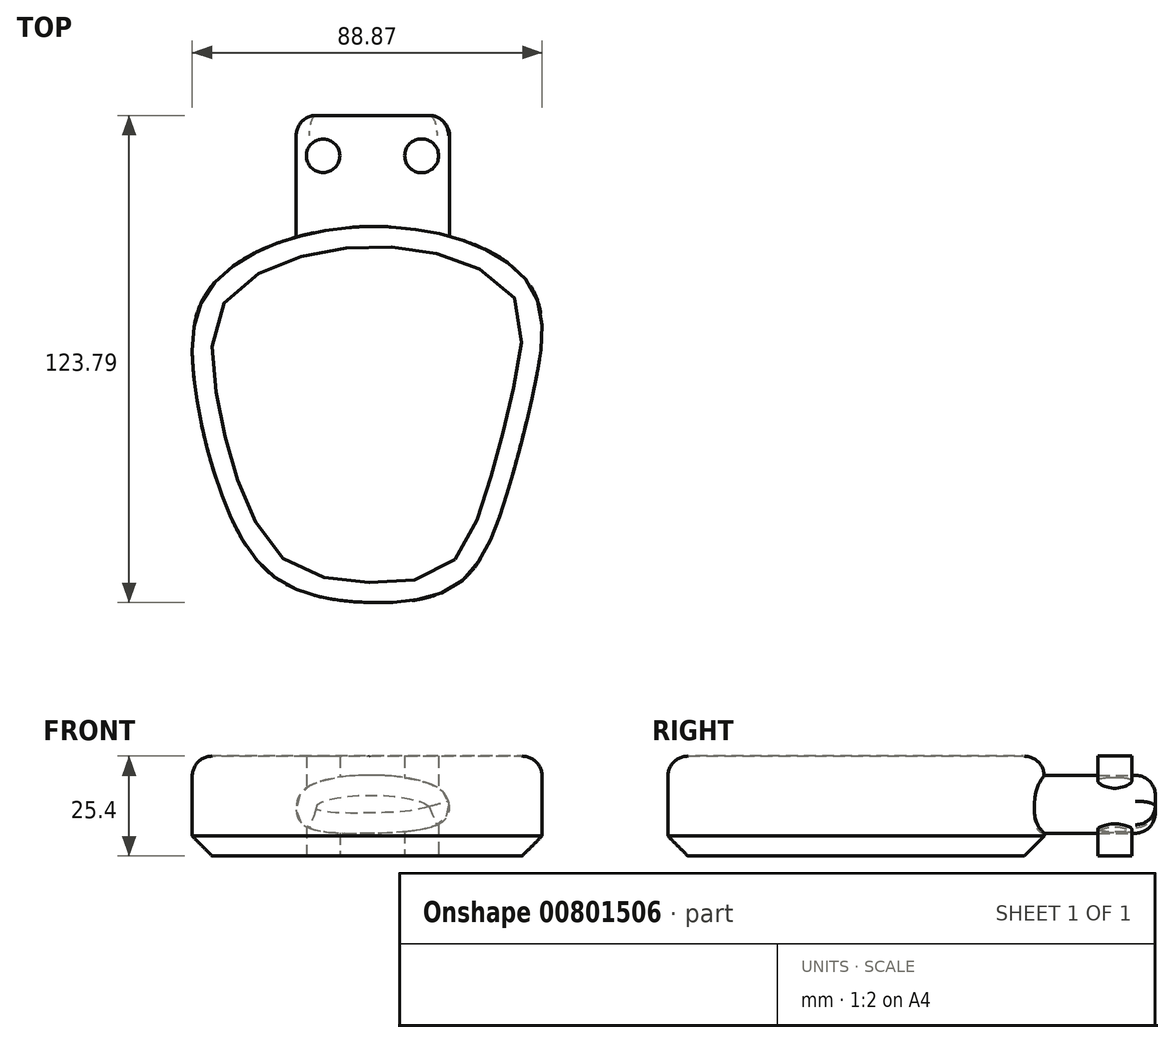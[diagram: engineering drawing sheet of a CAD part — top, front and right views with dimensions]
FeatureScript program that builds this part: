
annotation { "Feature Type Name" : "Feature", "Feature Type Description" : "" }
export const myFeature = defineFeature(function(context is Context, id is Id, definition is map)
    precondition{}
    {
        {
            var Q0;
            Q0=qCreatedBy(makeId("Top.planeOp"),FACE);
            var sketch = newSketch(context, id + "F0", { "sketchPlane" : qUnion([Q0])});
            skFitSpline(sketch, "E0", {"points": [v(0, -55.93) * mm, v(-24.36, -49.12) * mm, v(-38.24, -25.99) * mm, v(-44.22, 0) * mm, v(-40.41, 23.81) * mm, v(0, 39.6) * mm, v(40.69, 25.17) * mm, v(42.32, 0) * mm, v(34.97, -28.71) * mm, v(23.27, -50.75) * mm, v(0, -55.93) * mm]});
            skSolve(sketch);
        }
        {
            var Q0;
            Q0=makeQuery(id+"F0.imprint","IMPRINT",FACE,{"disambiguationData":[TD([[makeQuery(id+"F0.imprint","IMPRINT",EDGE,{"derivedFrom":sQuery(id+"F0.wireOp",EDGE,"E0")}),-1.0]])]});
            extrude(context, id + "F1", {"entities" : qUnion([Q0]), "depth" : 25.4 * mm, "offsetDistance" : 25.4 * mm});
        }
        {
            var Q0;
            Q0=makeQuery(id+"F1.opExtrude","CAP_EDGE",EDGE,{"disambiguationData":[OSD([sQuery(id+"F0.wireOp",EDGE,"E0")])],"isStart":false});
            fillet(context, id + "F2", {"entities" : qUnion([Q0]), "radius" : 5.08 * mm, "tangentPropagation" : true, "allowEdgeOverflow" : false});
        }
        {
            var Q0;
            Q0=makeQuery(id+"F1.opExtrude","CAP_EDGE",EDGE,{"disambiguationData":[OSD([sQuery(id+"F0.wireOp",EDGE,"E0")])],"isStart":true});
            chamfer(context, id + "F3", {"entities" : qUnion([Q0]), "width" : 5.08 * mm, "tangentPropagation" : true});
        }
        {
            var Q0;
            Q0=qCreatedBy(makeId("Front.planeOp"),FACE);
            var sketch = newSketch(context, id + "F4", { "sketchPlane" : qUnion([Q0])});
            skFitSpline(sketch, "E1", {"points": [v(0, 20.55) * mm, v(16.74, 17.83) * mm, v(20.27, 14.02) * mm, v(19.19, 9.12) * mm, v(0, 5.85) * mm, v(-16.74, 8.03) * mm, v(-18.37, 12.65) * mm, v(-15.92, 17.28) * mm, v(0, 20.55) * mm]});
            skSolve(sketch);
        }
        {
            var Q0;
            Q0 = qSketchRegion(id + "F4", true);
            extrude(context, id + "F5", {"entities" : qUnion([Q0]), "operationType" : NewBodyOperationType.ADD, "oppositeDirection" : true, "depth" : 67.82 * mm, "offsetDistance" : 25.4 * mm});
        }
        {
            var Q0;
            Q0=makeQuery(id+"F5.opExtrude","CAP_EDGE",EDGE,{"disambiguationData":[OSD([sQuery(id+"F4.wireOp",EDGE,"E1")])],"isStart":false});
            fillet(context, id + "F6", {"entities" : qUnion([Q0]), "radius" : 5.08 * mm, "tangentPropagation" : true, "allowEdgeOverflow" : false});
        }
        {
            var Q0;
            Q0=qCreatedBy(makeId("Top.planeOp"),FACE);
            var sketch = newSketch(context, id + "F7", { "sketchPlane" : qUnion([Q0])});
            skCircle(sketch, "E2", {"center": v(-11.57, 57.56) * mm, "radius": 4.25 * mm});
            skSolve(sketch);
        }
        {
            var Q0;
            Q0 = qSketchRegion(id + "F7", true);
            extrude(context, id + "F8", {"entities" : qUnion([Q0]), "operationType" : NewBodyOperationType.ADD, "depth" : 25.4 * mm, "offsetDistance" : 25.4 * mm});
        }
        {
            var Q0;
            Q0=qCreatedBy(makeId("Top.planeOp"),FACE);
            var sketch = newSketch(context, id + "F9", { "sketchPlane" : qUnion([Q0])});
            skCircle(sketch, "E3", {"center": v(13.47, 57.56) * mm, "radius": 4.3 * mm});
            skSolve(sketch);
        }
        {
            var Q0;
            Q0 = qSketchRegion(id + "F9", true);
            extrude(context, id + "F10", {"entities" : qUnion([Q0]), "operationType" : NewBodyOperationType.ADD, "depth" : 25.4 * mm, "offsetDistance" : 25.4 * mm});
        }
    });
